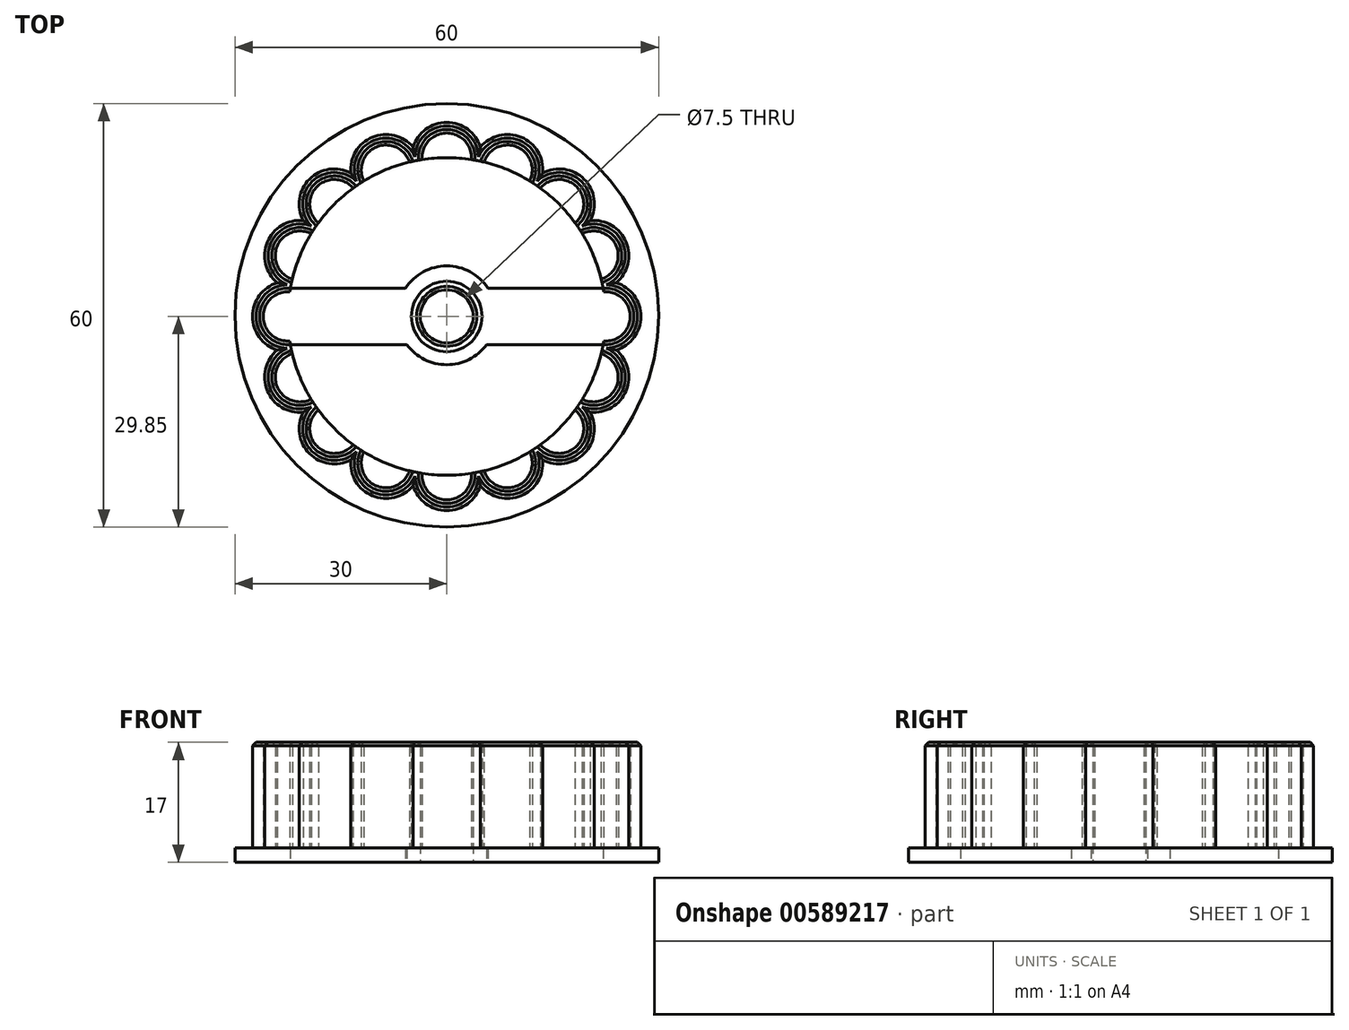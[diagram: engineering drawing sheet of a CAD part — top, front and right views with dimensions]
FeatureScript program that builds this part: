
annotation { "Feature Type Name" : "Feature", "Feature Type Description" : "" }
export const myFeature = defineFeature(function(context is Context, id is Id, definition is map)
    precondition{}
    {
        {
            var Q0;
            Q0=qCreatedBy(makeId("Top.planeOp"),FACE);
            var sketch = newSketch(context, id + "F0", { "sketchPlane" : qUnion([Q0]), "disableImprinting" : false});
            skCircle(sketch, "E0", {"center": v(0, 0.15) * mm, "radius": 30 * mm});
            skCircle(sketch, "E1", {"center": v(0, 0) * mm, "radius": 22.5 * mm});
            skArc(sketch, "E2", {"start": v(-5.63, -4) * mm, "mid": v(0, -6.85) * mm, "end": v(5.63, -4) * mm});
            skLineSegment(sketch, "E3.bottom", {"start": v(22.14, -4) * mm, "end": v(5.63, -4) * mm});
            skLineSegment(sketch, "E3.top", {"start": v(22.14, 4) * mm, "end": v(5.85, 4) * mm});
            skLineSegment(sketch, "E4.trimOffspring", {"start": v(-5.85, 4) * mm, "end": v(-22.14, 4) * mm});
            skLineSegment(sketch, "E5.trimOffspring", {"start": v(-5.63, -4) * mm, "end": v(-22.14, -4) * mm});
            skArc(sketch, "E6.trimOffspring", {"start": v(5.85, 4) * mm, "mid": v(0, 7.15) * mm, "end": v(-5.85, 4) * mm});
            skCircle(sketch, "E7", {"center": v(0, 0) * mm, "radius": 3.75 * mm});
            skSolve(sketch);
        }
        {
            var Q0;
            Q0=qSketchRegion(id+"F0",true);
            var Q1;
            Q1=makeQuery(id+"F0.imprint","IMPRINT",FACE,{"disambiguationData":[TD([[makeQuery(id+"F0.imprint","IMPRINT",EDGE,{"derivedFrom":sQuery(id+"F0.wireOp",EDGE,"E2")}),1.0]])]});
            extrude(context, id + "F1", {"entities" : qUnion([Q0, Q1]), "depth" : 2 * mm, "offsetDistance" : 25 * mm});
        }
        {
            var Q0;
            Q0=makeQuery(id+"F1.opExtrude","CAP_FACE",FACE,{"disambiguationData":[OSD([sQuery(id+"F0.wireOp",EDGE,"E0"),sQuery(id+"F0.wireOp",EDGE,"E1")])],"isStart":false});
            var sketch = newSketch(context, id + "F2", { "sketchPlane" : qUnion([Q0]), "disableImprinting" : false});
            skArc(sketch, "E8", {"start": v(3.49, -22.23) * mm, "mid": v(4.23, -22.1) * mm, "end": v(4.97, -21.94) * mm});
            skArc(sketch, "E9", {"start": v(-4.97, -21.94) * mm, "mid": v(0, -27.5) * mm, "end": v(4.97, -21.94) * mm});
            skArc(sketch, "E10.0", {"start": v(-3.49, -22.23) * mm, "mid": v(0, -26) * mm, "end": v(3.49, -22.23) * mm});
            skArc(sketch, "E11.trimOffspring", {"start": v(-4.97, -21.94) * mm, "mid": v(-4.23, -22.1) * mm, "end": v(-3.49, -22.23) * mm});
            skArc(sketch, "E12.1.0", {"start": v(3.8, -22.18) * mm, "mid": v(10.52, -25.4) * mm, "end": v(12.99, -18.37) * mm});
            skArc(sketch, "E12.1.1", {"start": v(5.28, -21.87) * mm, "mid": v(9.95, -24.02) * mm, "end": v(11.73, -19.2) * mm});
            skArc(sketch, "E12.2.0", {"start": v(12, -19.03) * mm, "mid": v(19.45, -19.45) * mm, "end": v(19.03, -12) * mm});
            skArc(sketch, "E12.2.1", {"start": v(13.25, -18.18) * mm, "mid": v(18.38, -18.38) * mm, "end": v(18.18, -13.25) * mm});
            skArc(sketch, "E12.3.0", {"start": v(18.37, -12.99) * mm, "mid": v(25.4, -10.52) * mm, "end": v(22.18, -3.8) * mm});
            skArc(sketch, "E12.3.1", {"start": v(19.2, -11.73) * mm, "mid": v(24.02, -9.95) * mm, "end": v(21.87, -5.28) * mm});
            skArc(sketch, "E12.4.0", {"start": v(21.94, -4.97) * mm, "mid": v(27.5, 0) * mm, "end": v(21.94, 4.97) * mm});
            skArc(sketch, "E12.4.1", {"start": v(22.23, -3.49) * mm, "mid": v(26, 0) * mm, "end": v(22.23, 3.49) * mm});
            skArc(sketch, "E12.5.0", {"start": v(22.18, 3.8) * mm, "mid": v(25.4, 10.52) * mm, "end": v(18.37, 12.99) * mm});
            skArc(sketch, "E12.5.1", {"start": v(21.87, 5.28) * mm, "mid": v(24.02, 9.95) * mm, "end": v(19.2, 11.73) * mm});
            skArc(sketch, "E12.6.0", {"start": v(19.03, 12) * mm, "mid": v(19.45, 19.45) * mm, "end": v(12, 19.03) * mm});
            skArc(sketch, "E12.6.1", {"start": v(18.18, 13.25) * mm, "mid": v(18.38, 18.38) * mm, "end": v(13.25, 18.18) * mm});
            skArc(sketch, "E12.7.0", {"start": v(12.99, 18.37) * mm, "mid": v(10.52, 25.4) * mm, "end": v(3.8, 22.18) * mm});
            skArc(sketch, "E12.7.1", {"start": v(11.73, 19.2) * mm, "mid": v(9.95, 24.02) * mm, "end": v(5.28, 21.87) * mm});
            skArc(sketch, "E12.8.0", {"start": v(4.97, 21.94) * mm, "mid": v(0, 27.5) * mm, "end": v(-4.97, 21.94) * mm});
            skArc(sketch, "E12.8.1", {"start": v(3.49, 22.23) * mm, "mid": v(0, 26) * mm, "end": v(-3.49, 22.23) * mm});
            skArc(sketch, "E12.9.0", {"start": v(-3.8, 22.18) * mm, "mid": v(-10.52, 25.4) * mm, "end": v(-12.99, 18.37) * mm});
            skArc(sketch, "E12.9.1", {"start": v(-5.28, 21.87) * mm, "mid": v(-9.95, 24.02) * mm, "end": v(-11.73, 19.2) * mm});
            skArc(sketch, "E12.10.0", {"start": v(-12, 19.03) * mm, "mid": v(-19.45, 19.45) * mm, "end": v(-19.03, 12) * mm});
            skArc(sketch, "E12.10.1", {"start": v(-13.25, 18.18) * mm, "mid": v(-18.38, 18.38) * mm, "end": v(-18.18, 13.25) * mm});
            skArc(sketch, "E12.11.0", {"start": v(-18.37, 12.99) * mm, "mid": v(-25.4, 10.52) * mm, "end": v(-22.18, 3.8) * mm});
            skArc(sketch, "E12.11.1", {"start": v(-19.2, 11.73) * mm, "mid": v(-24.02, 9.95) * mm, "end": v(-21.87, 5.28) * mm});
            skCircle(sketch, "E13", {"center": v(0, 0) * mm, "radius": 22.5 * mm});
            skArc(sketch, "E14.3.12.0", {"start": v(-21.94, 4.97) * mm, "mid": v(-27.5, 0) * mm, "end": v(-21.94, -4.97) * mm});
            skArc(sketch, "E14.4.12.0", {"start": v(-22.23, 3.49) * mm, "mid": v(-26, 0) * mm, "end": v(-22.23, -3.49) * mm});
            skArc(sketch, "E15.3.13.0", {"start": v(-22.18, -3.8) * mm, "mid": v(-25.4, -10.52) * mm, "end": v(-18.37, -12.99) * mm});
            skArc(sketch, "E15.4.13.0", {"start": v(-21.87, -5.28) * mm, "mid": v(-24.02, -9.95) * mm, "end": v(-19.2, -11.73) * mm});
            skArc(sketch, "E16.3.14.0", {"start": v(-19.03, -12) * mm, "mid": v(-19.45, -19.45) * mm, "end": v(-12, -19.03) * mm});
            skArc(sketch, "E16.4.14.0", {"start": v(-18.18, -13.25) * mm, "mid": v(-18.38, -18.38) * mm, "end": v(-13.25, -18.18) * mm});
            skArc(sketch, "E16.3.15.0", {"start": v(-12.99, -18.37) * mm, "mid": v(-10.52, -25.4) * mm, "end": v(-3.8, -22.18) * mm});
            skArc(sketch, "E16.4.15.0", {"start": v(-11.73, -19.2) * mm, "mid": v(-9.95, -24.02) * mm, "end": v(-5.28, -21.87) * mm});
            skCircle(sketch, "E17", {"center": v(0, 0) * mm, "radius": 5 * mm});
            skCircle(sketch, "E18.0", {"center": v(0, 0) * mm, "radius": 3.5 * mm});
            skSolve(sketch);
        }
        {
            var Q0;
            Q0=qSketchRegion(id+"F2",true);
            var Q1;
            Q1=makeQuery(id+"F2.imprint","IMPRINT",FACE,{"disambiguationData":[TD([[makeQuery(id+"F2.imprint","IMPRINT",EDGE,{"derivedFrom":sQuery(id+"F2.wireOp",EDGE,"E17")}),1.0]])]});
            extrude(context, id + "F3", {"entities" : qUnion([Q0, Q1]), "operationType" : NewBodyOperationType.ADD, "depth" : 15 * mm, "offsetDistance" : 25 * mm});
        }
        {
            var Q0;
            Q0=makeQuery(id+"F3.opExtrude","CAP_EDGE",EDGE,{"disambiguationData":[OSD([sQuery(id+"F2.wireOp",EDGE,"E12.9.0")])],"isStart":false});
            var Q1;
            Q1=makeQuery(id+"F3.opExtrude","CAP_EDGE",EDGE,{"disambiguationData":[OSD([sQuery(id+"F2.wireOp",EDGE,"E12.8.0")])],"isStart":false});
            var Q2;
            Q2=makeQuery(id+"F3.opExtrude","CAP_EDGE",EDGE,{"disambiguationData":[OSD([sQuery(id+"F2.wireOp",EDGE,"E12.7.0")])],"isStart":false});
            var Q3;
            Q3=makeQuery(id+"F3.opExtrude","CAP_EDGE",EDGE,{"disambiguationData":[OSD([sQuery(id+"F2.wireOp",EDGE,"E12.6.0")])],"isStart":false});
            var Q4;
            Q4=makeQuery(id+"F3.opExtrude","CAP_EDGE",EDGE,{"disambiguationData":[OSD([sQuery(id+"F2.wireOp",EDGE,"E12.5.0")])],"isStart":false});
            var Q5;
            Q5=makeQuery(id+"F3.opExtrude","CAP_EDGE",EDGE,{"disambiguationData":[OSD([sQuery(id+"F2.wireOp",EDGE,"E12.4.0")])],"isStart":false});
            var Q6;
            Q6=makeQuery(id+"F3.opExtrude","CAP_EDGE",EDGE,{"disambiguationData":[OSD([sQuery(id+"F2.wireOp",EDGE,"E12.3.0")])],"isStart":false});
            var Q7;
            Q7=makeQuery(id+"F3.opExtrude","CAP_EDGE",EDGE,{"disambiguationData":[OSD([sQuery(id+"F2.wireOp",EDGE,"E12.2.0")])],"isStart":false});
            var Q8;
            Q8=makeQuery(id+"F3.opExtrude","CAP_EDGE",EDGE,{"disambiguationData":[OSD([sQuery(id+"F2.wireOp",EDGE,"E12.1.0")])],"isStart":false});
            var Q9;
            Q9=makeQuery(id+"F3.opExtrude","CAP_EDGE",EDGE,{"disambiguationData":[OSD([sQuery(id+"F2.wireOp",EDGE,"E9")])],"isStart":false});
            var Q10;
            Q10=makeQuery(id+"F3.opExtrude","CAP_EDGE",EDGE,{"disambiguationData":[OSD([sQuery(id+"F2.wireOp",EDGE,"E16.3.15.0")])],"isStart":false});
            var Q11;
            Q11=makeQuery(id+"F3.opExtrude","CAP_EDGE",EDGE,{"disambiguationData":[OSD([sQuery(id+"F2.wireOp",EDGE,"E16.3.14.0")])],"isStart":false});
            var Q12;
            Q12=makeQuery(id+"F3.opExtrude","CAP_EDGE",EDGE,{"disambiguationData":[OSD([sQuery(id+"F2.wireOp",EDGE,"E15.3.13.0")])],"isStart":false});
            var Q13;
            Q13=makeQuery(id+"F3.opExtrude","CAP_EDGE",EDGE,{"disambiguationData":[OSD([sQuery(id+"F2.wireOp",EDGE,"E14.3.12.0")])],"isStart":false});
            var Q14;
            Q14=makeQuery(id+"F3.opExtrude","CAP_EDGE",EDGE,{"disambiguationData":[OSD([sQuery(id+"F2.wireOp",EDGE,"E12.11.0")])],"isStart":false});
            var Q15;
            Q15=makeQuery(id+"F3.opExtrude","CAP_EDGE",EDGE,{"disambiguationData":[OSD([sQuery(id+"F2.wireOp",EDGE,"E12.10.0")])],"isStart":false});
            var Q16;
            Q16=makeQuery(id+"F3.opExtrude","CAP_EDGE",EDGE,{"disambiguationData":[OSD([sQuery(id+"F2.wireOp",EDGE,"E12.10.1")])],"isStart":false});
            var Q17;
            Q17=makeQuery(id+"F3.opExtrude","CAP_EDGE",EDGE,{"disambiguationData":[OSD([sQuery(id+"F2.wireOp",EDGE,"E12.9.1")])],"isStart":false});
            var Q18;
            Q18=makeQuery(id+"F3.opExtrude","CAP_EDGE",EDGE,{"disambiguationData":[OSD([sQuery(id+"F2.wireOp",EDGE,"E12.8.1")])],"isStart":false});
            var Q19;
            Q19=makeQuery(id+"F3.opExtrude","CAP_EDGE",EDGE,{"disambiguationData":[OSD([sQuery(id+"F2.wireOp",EDGE,"E12.7.1")])],"isStart":false});
            var Q20;
            Q20=makeQuery(id+"F3.opExtrude","CAP_EDGE",EDGE,{"disambiguationData":[OSD([sQuery(id+"F2.wireOp",EDGE,"E12.6.1")])],"isStart":false});
            var Q21;
            Q21=makeQuery(id+"F3.opExtrude","CAP_EDGE",EDGE,{"disambiguationData":[OSD([sQuery(id+"F2.wireOp",EDGE,"E12.5.1")])],"isStart":false});
            var Q22;
            Q22=makeQuery(id+"F3.opExtrude","CAP_EDGE",EDGE,{"disambiguationData":[OSD([sQuery(id+"F2.wireOp",EDGE,"E12.4.1")])],"isStart":false});
            var Q23;
            Q23=makeQuery(id+"F3.opExtrude","CAP_EDGE",EDGE,{"disambiguationData":[OSD([sQuery(id+"F2.wireOp",EDGE,"E12.3.1")])],"isStart":false});
            var Q24;
            Q24=makeQuery(id+"F3.opExtrude","CAP_EDGE",EDGE,{"disambiguationData":[OSD([sQuery(id+"F2.wireOp",EDGE,"E12.2.1")])],"isStart":false});
            var Q25;
            Q25=makeQuery(id+"F3.opExtrude","CAP_EDGE",EDGE,{"disambiguationData":[OSD([sQuery(id+"F2.wireOp",EDGE,"E12.1.1")])],"isStart":false});
            var Q26;
            Q26=makeQuery(id+"F3.opExtrude","CAP_EDGE",EDGE,{"disambiguationData":[OSD([sQuery(id+"F2.wireOp",EDGE,"E10.0")])],"isStart":false});
            var Q27;
            Q27=makeQuery(id+"F3.opExtrude","CAP_EDGE",EDGE,{"disambiguationData":[OSD([sQuery(id+"F2.wireOp",EDGE,"E16.4.15.0")])],"isStart":false});
            var Q28;
            Q28=makeQuery(id+"F3.opExtrude","CAP_EDGE",EDGE,{"disambiguationData":[OSD([sQuery(id+"F2.wireOp",EDGE,"E16.4.14.0")])],"isStart":false});
            var Q29;
            Q29=makeQuery(id+"F3.opExtrude","CAP_EDGE",EDGE,{"disambiguationData":[OSD([sQuery(id+"F2.wireOp",EDGE,"E15.4.13.0")])],"isStart":false});
            var Q30;
            Q30=makeQuery(id+"F3.opExtrude","CAP_EDGE",EDGE,{"disambiguationData":[OSD([sQuery(id+"F2.wireOp",EDGE,"E14.4.12.0")])],"isStart":false});
            var Q31;
            Q31=makeQuery(id+"F3.opExtrude","CAP_EDGE",EDGE,{"disambiguationData":[OSD([sQuery(id+"F2.wireOp",EDGE,"E12.11.1")])],"isStart":false});
            var Q32;
            Q32=makeQuery(id+"F3.opExtrude","CAP_EDGE",EDGE,{"disambiguationData":[OSD([sQuery(id+"F0.wireOp",EDGE,"E7")])],"isStart":false});
            chamfer(context, id + "F4", {"entities" : qUnion([Q0, Q1, Q2, Q3, Q4, Q5, Q6, Q7, Q8, Q9, Q10, Q11, Q12, Q13, Q14, Q15, Q16, Q17, Q18, Q19, Q20, Q21, Q22, Q23, Q24, Q25, Q26, Q27, Q28, Q29, Q30, Q31, Q32]), "width" : .5 * mm, "tangentPropagation" : true});
        }
    });
